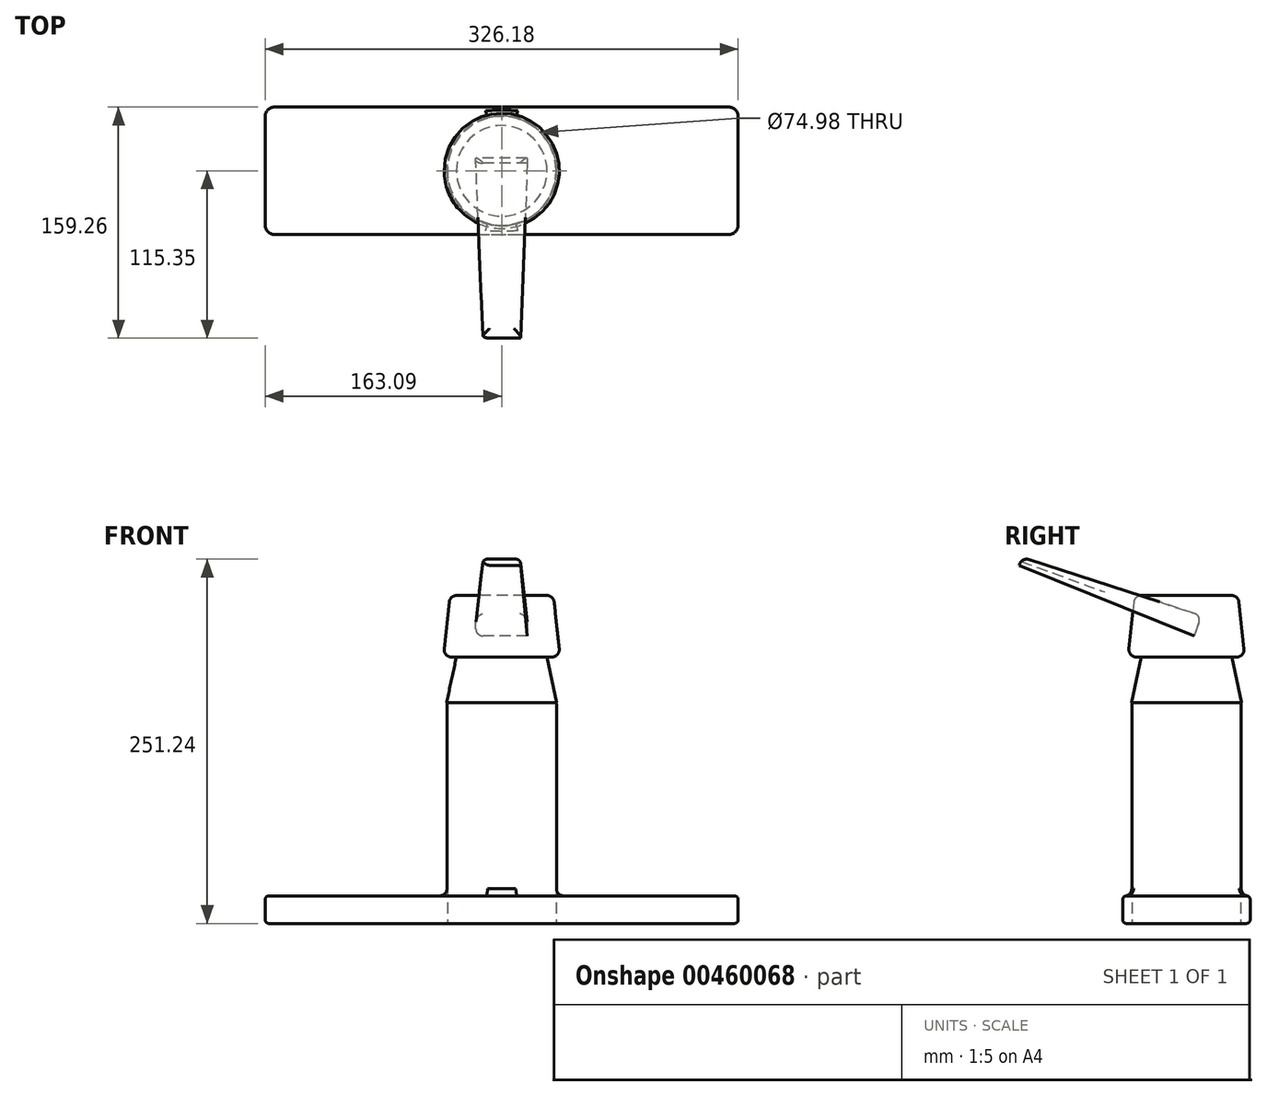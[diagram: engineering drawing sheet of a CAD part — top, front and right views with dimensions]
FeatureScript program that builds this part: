
annotation { "Feature Type Name" : "Feature", "Feature Type Description" : "" }
export const myFeature = defineFeature(function(context is Context, id is Id, definition is map)
    precondition{}
    {
        {
            var Q0;
            Q0=qCreatedBy(makeId("Top.planeOp"),FACE);
            var sketch = newSketch(context, id + "F0", { "sketchPlane" : qUnion([Q0])});
            skLineSegment(sketch, "E0.bottom", {"start": v(-156.74, 43.9) * mm, "end": v(156.74, 43.9) * mm});
            skLineSegment(sketch, "E0.top", {"start": v(-156.74, -43.9) * mm, "end": v(156.74, -43.9) * mm});
            skLineSegment(sketch, "E0.left", {"start": v(-163.09, 37.56) * mm, "end": v(-163.09, -37.56) * mm});
            skLineSegment(sketch, "E0.right", {"start": v(163.09, 37.56) * mm, "end": v(163.09, -37.56) * mm});
            skPoint(sketch, "E0.middle", {"position": v(0, 0) * mm});
            skCircle(sketch, "E1", {"center": v(0, 0) * mm, "radius": 37.74 * mm});
            skPoint(sketch, "E2.visualSharp", {"position": v(-163.09, 43.9) * mm});
            skArc(sketch, "E2.filletArc", {"start": v(-156.74, 43.9) * mm, "mid": v(-161.23, 42.05) * mm, "end": v(-163.09, 37.56) * mm});
            skLineSegment(sketch, "E3", {"start": v(-163.09, 0) * mm, "end": v(163.09, 0) * mm, "construction": true});
            skLineSegment(sketch, "E4", {"start": v(0, 43.9) * mm, "end": v(0, -43.9) * mm, "construction": true});
            skPoint(sketch, "E4.startSnap0", {"position": v(3.17, 43.9) * mm});
            skPoint(sketch, "E5.MirrorP", {"position": v(163.09, 43.9) * mm});
            skArc(sketch, "E6.filletArc", {"start": v(163.09, 37.56) * mm, "mid": v(161.23, 42.05) * mm, "end": v(156.74, 43.9) * mm});
            skPoint(sketch, "E7.visualSharp", {"position": v(-163.09, -43.9) * mm});
            skArc(sketch, "E7.filletArc", {"start": v(-163.09, -37.56) * mm, "mid": v(-161.23, -42.05) * mm, "end": v(-156.74, -43.9) * mm});
            skPoint(sketch, "E8.visualSharp", {"position": v(163.09, -43.9) * mm});
            skArc(sketch, "E8.filletArc", {"start": v(156.74, -43.9) * mm, "mid": v(161.23, -42.05) * mm, "end": v(163.09, -37.56) * mm});
            skSolve(sketch);
        }
        {
            var Q0;
            Q0=makeQuery(id+"F0.imprint","IMPRINT",FACE,{"disambiguationData":[TD([[makeQuery(id+"F0.imprint","IMPRINT",EDGE,{"derivedFrom":sQuery(id+"F0.wireOp",EDGE,"E1")}),1.0]])]});
            var Q1;
            Q1=sQuery(id+"F0.wireOp",EDGE,"E1");
            extrude(context, id + "F1", {"entities" : qUnion([Q0]), "bodyType" : ToolBodyType.SURFACE, "surfaceEntities" : qUnion([Q1]), "depth" : 38.1 * mm});
        }
        {
            var Q0;
            Q0 = qSketchRegion(id + "F0", true);
            extrude(context, id + "F2", {"entities" : qUnion([Q0]), "depth" : 19.05 * mm});
        }
        {
            var Q0;
            Q0=makeQuery(id+"F2.opExtrude","CAP_FACE",FACE,{"disambiguationData":[OSD([sQuery(id+"F0.wireOp",EDGE,"E0.bottom"),sQuery(id+"F0.wireOp",EDGE,"E0.top"),sQuery(id+"F0.wireOp",EDGE,"E0.left"),sQuery(id+"F0.wireOp",EDGE,"E0.right"),sQuery(id+"F0.wireOp",EDGE,"E1"),sQuery(id+"F0.wireOp",EDGE,"E2.filletArc"),sQuery(id+"F0.wireOp",EDGE,"E6.filletArc"),sQuery(id+"F0.wireOp",EDGE,"E7.filletArc"),sQuery(id+"F0.wireOp",EDGE,"E8.filletArc")])],"isStart":false});
            var Q1;
            Q1=makeQuery(id+"F2.opExtrude","CAP_EDGE",EDGE,{"disambiguationData":[OSD([sQuery(id+"F0.wireOp",EDGE,"E0.top")])],"isStart":true});
            fillet(context, id + "F3", {"entities" : qUnion([Q0, Q1]), "radius" : 2.54 * mm, "tangentPropagation" : true, "allowEdgeOverflow" : false});
        }
        {
            var Q0;
            Q0=qCreatedBy(makeId("Top.planeOp"),FACE);
            var sketch = newSketch(context, id + "F4", { "sketchPlane" : qUnion([Q0])});
            skCircle(sketch, "E9", {"center": v(0, 0) * mm, "radius": 35.18 * mm});
            skSolve(sketch);
        }
        {
            var Q0;
            Q0 = qSketchRegion(id + "F4", true);
            var Q1;
            Q1 = qConstructionFilter(qBodyType(qCreatedBy(id + "F4" ,EDGE), BodyType.WIRE), ConstructionObject.NO);
            extrude(context, id + "F5", {"entities" : qUnion([Q0]), "bodyType" : ToolBodyType.SURFACE, "surfaceEntities" : qUnion([Q1]), "depth" : 127 * mm});
        }
        {
            var Q0;
            Q0=qCreatedBy(makeId("Top.planeOp"),FACE);
            var sketch = newSketch(context, id + "F6", { "sketchPlane" : qUnion([Q0])});
            skCircle(sketch, "E10.0", {"center": v(0, 0) * mm, "radius": 37.74 * mm});
            skCircle(sketch, "E11", {"center": v(0, 0) * mm, "radius": 37.5 * mm});
            skSolve(sketch);
        }
        {
            var Q0;
            Q0 = qSketchRegion(id + "F6", true);
            extrude(context, id + "F7", {"entities" : qUnion([Q0]), "operationType" : NewBodyOperationType.ADD, "depth" : 152.4 * mm});
        }
        {
            var Q0;
            Q0=qCreatedBy(makeId("Front.planeOp"),FACE);
            var sketch = newSketch(context, id + "F8", { "sketchPlane" : qUnion([Q0])});
            skCircle(sketch, "E12", {"center": v(0, 79.78) * mm, "radius": 27.94 * mm});
            skSolve(sketch);
        }
        {
            var Q0;
            Q0 = qSketchRegion(id + "F8", true);
            var Q1;
            Q1=sQuery(id+"F8.wireOp",EDGE,"E12");
            extrude(context, id + "F9", {"entities" : qUnion([Q0]), "bodyType" : ToolBodyType.SURFACE, "operationType" : NewBodyOperationType.ADD, "surfaceEntities" : qUnion([Q1]), "depth" : 101.6 * mm, "hasSecondDirection" : true, "secondDirectionOppositeDirection" : false, "secondDirectionDepth" : 18.8 * mm});
        }
        {
            var Q0;
            Q0=qCreatedBy(makeId("Front.planeOp"),FACE);
            var sketch = newSketch(context, id + "F10", { "sketchPlane" : qUnion([Q0])});
            skLineSegment(sketch, "E13", {"start": v(0, 0) * mm, "end": v(0, 151.68) * mm, "construction": true});
            skSolve(sketch);
        }
        {
            var Q0;
            Q0=qCreatedBy(makeId("Front.planeOp"),FACE);
            var sketch = newSketch(context, id + "F11", { "sketchPlane" : qUnion([Q0])});
            skLineSegment(sketch, "E14", {"start": v(38.11, 83.49) * mm, "end": v(-35, 83.49) * mm, "construction": true});
            skSolve(sketch);
        }
        {
            var Q0;
            Q0=makeQuery(id+"F9.opExtrude","SWEPT_BODY",BODY,{"disambiguationData":[OSD([sQuery(id+"F8.wireOp",EDGE,"E12")])]});
            var Q1;
            Q1=sQuery(id+"F11.wireOp",EDGE,"E14");
            transform(context, id + "F12", {"entities" : qUnion([Q0]), "transformType" : TransformType.ROTATION, "transformAxis" : qUnion([Q1]), "angle" : 20 * degree, "makeCopy" : false});
        }
        {
            var Q0;
            Q0=qCreatedBy(makeId("Front.planeOp"),FACE);
            var sketch = newSketch(context, id + "F13", { "sketchPlane" : qUnion([Q0])});
            skLineSegment(sketch, "E15", {"start": v(0, 152.43) * mm, "end": v(-38, 152.43) * mm});
            skLineSegment(sketch, "E16", {"start": v(-38, 152.43) * mm, "end": v(-27.76, 200.05) * mm});
            skLineSegment(sketch, "E17", {"start": v(-27.76, 200.05) * mm, "end": v(0, 200.05) * mm});
            skLineSegment(sketch, "E18", {"start": v(0, 200.05) * mm, "end": v(0, 152.43) * mm});
            skSolve(sketch);
        }
        {
            var Q0;
            Q0=makeQuery(id+"F13.imprint","IMPRINT",FACE,{"disambiguationData":[TD([[makeQuery(id+"F13.imprint","IMPRINT",EDGE,{"derivedFrom":sQuery(id+"F13.wireOp",EDGE,"E15")}),-1.0]])]});
            var Q1;
            Q1=sQuery(id+"F13.wireOp",EDGE,"E16");
            var Q2;
            Q2=sQuery(id+"F13.wireOp",EDGE,"E15");
            var Q3;
            Q3=sQuery(id+"F13.wireOp",EDGE,"E18");
            var Q4;
            Q4=sQuery(id+"F13.wireOp",EDGE,"E17");
            var Q5;
            Q5=sQuery(id+"F13.wireOp",EDGE,"E18");
            revolve(context, id + "F14", {"entities" : qUnion([Q0]), "surfaceEntities" : qUnion([Q1, Q2, Q3, Q4]), "axis" : qUnion([Q5]), "revolveType" : RevolveType.FULL});
        }
        {
            var Q0;
            Q0=qCreatedBy(makeId("Front.planeOp"),FACE);
            var sketch = newSketch(context, id + "F15", { "sketchPlane" : qUnion([Q0])});
            skLineSegment(sketch, "E19", {"start": v(0, 183.71) * mm, "end": v(-40.29, 183.71) * mm});
            skLineSegment(sketch, "E20", {"start": v(-40.29, 183.71) * mm, "end": v(-35.67, 226.23) * mm});
            skLineSegment(sketch, "E21", {"start": v(-35.67, 226.23) * mm, "end": v(0, 226.23) * mm});
            skLineSegment(sketch, "E22", {"start": v(0, 226.23) * mm, "end": v(0, 183.71) * mm});
            skSolve(sketch);
        }
        {
            var Q0;
            Q0=makeQuery(id+"F15.imprint","IMPRINT",FACE,{"disambiguationData":[TD([[makeQuery(id+"F15.imprint","IMPRINT",EDGE,{"derivedFrom":sQuery(id+"F15.wireOp",EDGE,"E19")}),-1.0]])]});
            var Q1;
            Q1=sQuery(id+"F10.wireOp",EDGE,"E13");
            revolve(context, id + "F16", {"operationType" : NewBodyOperationType.ADD, "entities" : qUnion([Q0]), "axis" : qUnion([Q1]), "revolveType" : RevolveType.FULL});
        }
        {
            var Q0;
            Q0=qCreatedBy(makeId("Front.planeOp"),FACE);
            var sketch = newSketch(context, id + "F17", { "sketchPlane" : qUnion([Q0])});
            skLineSegment(sketch, "E23.bottom", {"start": v(-17.84, 214.13) * mm, "end": v(17.66, 214.13) * mm});
            skLineSegment(sketch, "E23.top", {"start": v(-17.84, 199.2) * mm, "end": v(17.66, 199.2) * mm});
            skLineSegment(sketch, "E23.left", {"start": v(-17.84, 214.13) * mm, "end": v(-17.84, 199.2) * mm});
            skLineSegment(sketch, "E23.right", {"start": v(17.66, 214.13) * mm, "end": v(17.66, 199.2) * mm});
            skLineSegment(sketch, "E24", {"start": v(-17.84, 206.67) * mm, "end": v(17.66, 206.67) * mm, "construction": true});
            skSolve(sketch);
        }
        {
            var Q0;
            Q0 = qSketchRegion(id + "F17", true);
            extrude(context, id + "F18", {"entities" : qUnion([Q0]), "depth" : 130.05 * mm, "hasDraft" : true, "draftAngle" : 2 * degree, "draftPullDirection" : true});
        }
        {
            var Q0;
            Q0=makeQuery(id+"F18.opExtrude","SWEPT_BODY",BODY,{"disambiguationData":[OSD([sQuery(id+"F17.wireOp",EDGE,"E23.bottom"),sQuery(id+"F17.wireOp",EDGE,"E23.top"),sQuery(id+"F17.wireOp",EDGE,"E23.left"),sQuery(id+"F17.wireOp",EDGE,"E23.right")])]});
            var Q1;
            Q1=sQuery(id+"F15.wireOp",EDGE,"E19");
            transform(context, id + "F19", {"entities" : qUnion([Q0]), "transformType" : TransformType.ROTATION, "transformAxis" : qUnion([Q1]), "angle" : 20 * degree, "makeCopy" : false});
        }
        {
            var Q0;
            Q0=qCreatedBy(makeId("Right.planeOp"),FACE);
            var sketch = newSketch(context, id + "F20", { "sketchPlane" : qUnion([Q0])});
            skLineSegment(sketch, "E25", {"start": v(0, 0) * mm, "end": v(-120.43, 0) * mm});
            skLineSegment(sketch, "E26", {"start": v(-120.43, 0) * mm, "end": v(0, 0) * mm});
            skLineSegment(sketch, "E27", {"start": v(0, 0) * mm, "end": v(-36.67, -100.75) * mm});
            skSolve(sketch);
        }
        {
            var Q0;
            Q0=qCreatedBy(makeId("Front.planeOp"),FACE);
            var Q1;
            Q1=sQuery(id+"F20.wireOp",EDGE,"E27");
            cPlane(context, id + "F21", {"entities" : qUnion([Q0, Q1]), "cplaneType" : CPlaneType.LINE_ANGLE, "offset" : 25.4 * mm, "angle" : 0 * degree, "width" : 152.4 * mm, "height" : 152.4 * mm});
        }
        {
            var Q0;
            Q0=qCreatedBy(id+"F21.planeOp",FACE);
            cPlane(context, id + "F22", {"entities" : qUnion([Q0]), "cplaneType" : CPlaneType.OFFSET, "offset" : 98.55 * mm, "oppositeDirection" : true, "width" : 152.4 * mm, "height" : 152.4 * mm});
        }
        {
            var Q0;
            Q0=qCreatedBy(id+"F22.planeOp",FACE);
            var sketch = newSketch(context, id + "F23", { "sketchPlane" : qUnion([Q0])});
            skCircle(sketch, "E28", {"center": v(0, 75.31) * mm, "radius": 26.5 * mm});
            skSolve(sketch);
        }
        {
            var Q0;
            Q0=qCreatedBy(makeId("Right.planeOp"),FACE);
            var sketch = newSketch(context, id + "F24", { "sketchPlane" : qUnion([Q0])});
            skFitSpline(sketch, "E29", {"points": [v(-30.34, 87.73) * mm, v(-170.12, 135.42) * mm, v(-249.59, 136.95) * mm], "startDerivative": vector(-291.12, 163.3) * mm, "endDerivative": vector(-240.6, -23.16) * mm});
            skSolve(sketch);
        }
        {
            var Q0;
            Q0 = qSketchRegion(id + "F23", true);
            var Q1;
            Q1=sQuery(id+"F23.wireOp",EDGE,"E28");
            var Q2;
            Q2=sQuery(id+"F24.wireOp",EDGE,"otEZL0sl-9XYc-qNy6-Q2Yl-TIyQWOSTfNdC");
            var Q3;
            Q3=sQuery(id+"F24.wireOp",EDGE,"E29");
            sweep(context, id + "F25", {"bodyType" : ToolBodyType.SURFACE, "profiles" : qUnion([Q0]), "surfaceProfiles" : qUnion([Q1, Q2]), "path" : qUnion([Q3])});
        }
        {
            var Q0;
            Q0=qCreatedBy(makeId("Right.planeOp"),FACE);
            var sketch = newSketch(context, id + "F26", { "sketchPlane" : qUnion([Q0])});
            skLineSegment(sketch, "E30", {"start": v(-302.37, 169.55) * mm, "end": v(-280.41, 169.55) * mm});
            skLineSegment(sketch, "E31", {"start": v(-280.41, 169.55) * mm, "end": v(-265.4, 149.32) * mm});
            skLineSegment(sketch, "E32", {"start": v(-265.4, 149.32) * mm, "end": v(-265.4, 88.07) * mm});
            skLineSegment(sketch, "E33", {"start": v(-265.4, 88.07) * mm, "end": v(-301.8, 88.07) * mm});
            skLineSegment(sketch, "E34", {"start": v(-301.8, 88.07) * mm, "end": v(-302.37, 169.55) * mm});
            skSolve(sketch);
        }
        {
            var Q0;
            Q0=sQuery(id+"F26.wireOp",EDGE,"E32");
            var Q1;
            Q1=sQuery(id+"F26.wireOp",EDGE,"E31");
            var Q2;
            Q2=sQuery(id+"F26.wireOp",EDGE,"E30");
            var Q3;
            Q3=sQuery(id+"F26.wireOp",EDGE,"E33");
            var Q4;
            Q4=sQuery(id+"F26.wireOp",EDGE,"E34");
            revolve(context, id + "F27", {"bodyType" : ToolBodyType.SURFACE, "surfaceEntities" : qUnion([Q0, Q1, Q2, Q3]), "axis" : qUnion([Q4]), "revolveType" : RevolveType.FULL});
        }
        {
            var Q0;
            Q0=makeQuery(id+"F27.opRevolve","SWEPT_EDGE",EDGE,{"disambiguationData":[OSD([sQuery(id+"F26.wireOp",VERTEX,"E30.end")])]});
            fillet(context, id + "F28", {"entities" : qUnion([Q0]), "radius" : 0.08 * mm, "tangentPropagation" : true, "allowEdgeOverflow" : false});
        }
        {
            var Q0;
            Q0=makeQuery(id+"F18.opExtrude","SWEPT_FACE",FACE,{"disambiguationData":[OSD([sQuery(id+"F17.wireOp",EDGE,"E23.bottom")])]});
            var Q1;
            Q1=makeQuery(id+"F18.opExtrude","SWEPT_EDGE",EDGE,{"disambiguationData":[OSD([sQuery(id+"F17.wireOp",EDGE,"E23.top"),sQuery(id+"F17.wireOp",EDGE,"E23.left")])]});
            fillet(context, id + "F29", {"entities" : qUnion([Q0, Q1]), "radius" : 5.08 * mm, "tangentPropagation" : true, "allowEdgeOverflow" : false});
        }
        {
            var Q0;
            Q0=makeQuery(id+"F16.opRevolve","SWEPT_FACE",FACE,{"disambiguationData":[OSD([sQuery(id+"F15.wireOp",EDGE,"E21")])]});
            var Q1;
            Q1=makeQuery(id+"F16.opRevolve","SWEPT_FACE",FACE,{"disambiguationData":[OSD([sQuery(id+"F15.wireOp",EDGE,"E20")])]});
            fillet(context, id + "F30", {"entities" : qUnion([Q0, Q1]), "radius" : 5.08 * mm, "tangentPropagation" : true, "allowEdgeOverflow" : false});
        }
        {
            var Q0;
            Q0=makeQuery(id+"F27.opRevolve","SWEPT_FACE",FACE,{"disambiguationData":[OSD([sQuery(id+"F26.wireOp",EDGE,"E30")])]});
            var Q1;
            Q1=makeQuery(id+"F27.opRevolve","SWEPT_FACE",FACE,{"disambiguationData":[OSD([sQuery(id+"F26.wireOp",EDGE,"E31")])]});
            var Q2;
            Q2=makeQuery(id+"F27.opRevolve","SWEPT_FACE",FACE,{"disambiguationData":[OSD([sQuery(id+"F26.wireOp",EDGE,"E32")])]});
            fillet(context, id + "F31", {"entities" : qUnion([Q0, Q1, Q2]), "radius" : 5.08 * mm, "tangentPropagation" : true, "allowEdgeOverflow" : false});
        }
        {
            var Q0;
            Q0=makeQuery(id+"F7.opExtrude","SWEPT_FACE",FACE,{"disambiguationData":[OSD([sQuery(id+"F6.wireOp",EDGE,"E10.0")])]});
            var Q1;
            Q1=makeQuery(id+"F1.opExtrude","SWEPT_FACE",FACE,{"disambiguationData":[OSD([sQuery(id+"F0.wireOp",EDGE,"E1")])]});
            fillet(context, id + "F32", {"entities" : qUnion([Q0, Q1]), "radius" : 5.08 * mm, "tangentPropagation" : true, "allowEdgeOverflow" : false});
        }
    });
